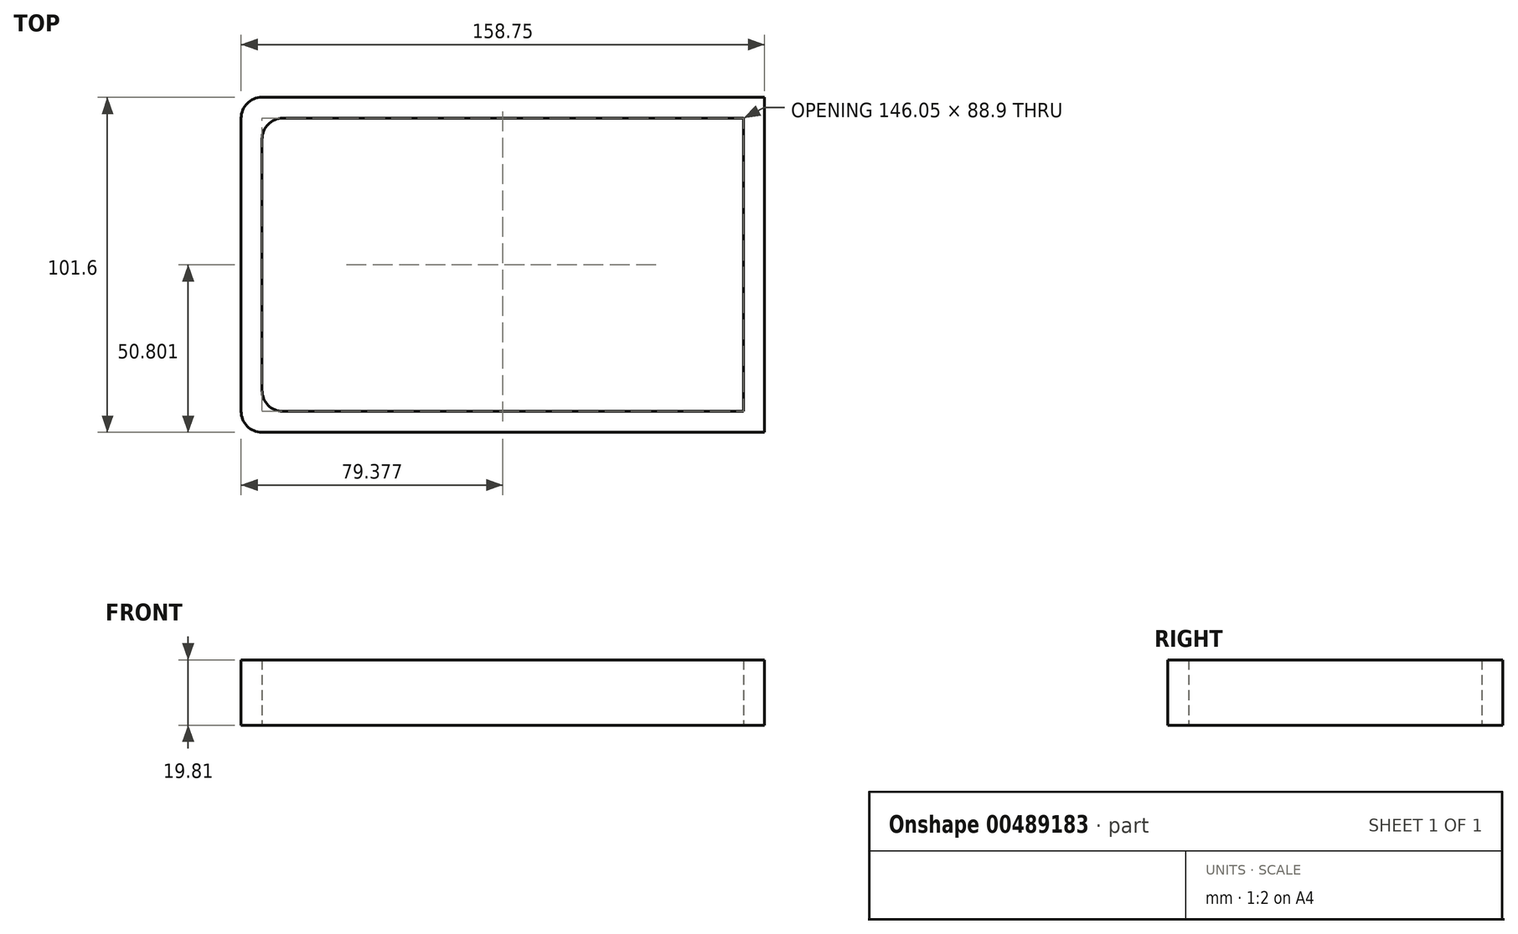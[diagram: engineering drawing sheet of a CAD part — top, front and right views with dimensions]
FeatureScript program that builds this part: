
annotation { "Feature Type Name" : "Feature", "Feature Type Description" : "" }
export const myFeature = defineFeature(function(context is Context, id is Id, definition is map)
    precondition{}
    {
        {
            var Q0;
            Q0=qCreatedBy(makeId("Top.planeOp"),FACE);
            var sketch = newSketch(context, id + "F0", { "sketchPlane" : qUnion([Q0])});
            skLineSegment(sketch, "E0.bottom", {"start": v(-53.38, 55.6) * mm, "end": v(105.37, 55.6) * mm});
            skLineSegment(sketch, "E0.top", {"start": v(-53.38, -46) * mm, "end": v(105.37, -46) * mm});
            skLineSegment(sketch, "E0.left", {"start": v(-53.38, 55.6) * mm, "end": v(-53.38, -46) * mm});
            skLineSegment(sketch, "E0.right", {"start": v(105.37, 55.6) * mm, "end": v(105.37, -46) * mm});
            skLineSegment(sketch, "E1", {"start": v(-53.38, -46) * mm, "end": v(-47.03, -46) * mm, "construction": true});
            skLineSegment(sketch, "E2", {"start": v(-53.38, -46) * mm, "end": v(-53.38, -39.66) * mm, "construction": true});
            skArc(sketch, "E3", {"start": v(-53.38, -39.66) * mm, "mid": v(-51.52, -44.15) * mm, "end": v(-47.03, -46) * mm});
            skLineSegment(sketch, "E4", {"start": v(-53.38, 55.6) * mm, "end": v(-53.38, 49.24) * mm, "construction": true});
            skLineSegment(sketch, "E5", {"start": v(-53.38, 55.6) * mm, "end": v(-47.03, 55.6) * mm, "construction": true});
            skArc(sketch, "E6", {"start": v(-47.03, 55.6) * mm, "mid": v(-51.52, 53.73) * mm, "end": v(-53.38, 49.24) * mm});
            skLineSegment(sketch, "E7", {"start": v(-28.06, 55.6) * mm, "end": v(-28.06, 49.24) * mm, "construction": true});
            skLineSegment(sketch, "E8", {"start": v(-51.52, 53.73) * mm, "end": v(-47.03, 49.24) * mm, "construction": true});
            skLineSegment(sketch, "E9.0", {"start": v(-47.03, 49.24) * mm, "end": v(99.02, 49.24) * mm});
            skLineSegment(sketch, "E9.1", {"start": v(-47.03, 49.24) * mm, "end": v(-47.03, -39.66) * mm});
            skLineSegment(sketch, "E9.2", {"start": v(-47.03, -39.66) * mm, "end": v(99.02, -39.66) * mm});
            skLineSegment(sketch, "E9.3", {"start": v(99.02, 49.24) * mm, "end": v(99.02, -39.66) * mm});
            skLineSegment(sketch, "E10", {"start": v(-47.03, 49.24) * mm, "end": v(-40.68, 49.24) * mm, "construction": true});
            skLineSegment(sketch, "E11", {"start": v(-47.03, 49.24) * mm, "end": v(-47.03, 42.9) * mm, "construction": true});
            skArc(sketch, "E12", {"start": v(-40.68, 49.24) * mm, "mid": v(-45.17, 47.38) * mm, "end": v(-47.03, 42.9) * mm});
            skLineSegment(sketch, "E13", {"start": v(-47.03, -39.66) * mm, "end": v(-40.68, -39.66) * mm, "construction": true});
            skLineSegment(sketch, "E14", {"start": v(-47.03, -39.66) * mm, "end": v(-47.03, -33.3) * mm, "construction": true});
            skArc(sketch, "E15", {"start": v(-47.03, -33.3) * mm, "mid": v(-45.17, -37.8) * mm, "end": v(-40.68, -39.66) * mm});
            skSolve(sketch);
        }
        {
            var Q0;
            {var subQ0=sQuery(id+"F0.wireOp",EDGE,"E0.right");Q0=makeQuery(id+"F0.imprint","IMPRINT",FACE,{"disambiguationData":[TD([[makeQuery(id+"F0.imprint","IMPRINT",EDGE,{"derivedFrom":subQ0}),-1.0]])]});}
            var Q1;
            {var subQ3=sQuery(id+"F0.wireOp",EDGE,"E12");Q1=makeQuery(id+"F0.imprint","IMPRINT",FACE,{"disambiguationData":[TD([[makeQuery(id+"F0.imprint","IMPRINT",EDGE,{"derivedFrom":subQ3}),-1.0]])]});}
            var Q2;
            {var subQ3=sQuery(id+"F0.wireOp",EDGE,"E15");Q2=makeQuery(id+"F0.imprint","IMPRINT",FACE,{"disambiguationData":[TD([[makeQuery(id+"F0.imprint","IMPRINT",EDGE,{"derivedFrom":subQ3}),-1.0]])]});}
            extrude(context, id + "F1", {"entities" : qUnion([Q0, Q1, Q2]), "depth" : 19.8 * mm, "offsetDistance" : 25.4 * mm});
        }
    });
